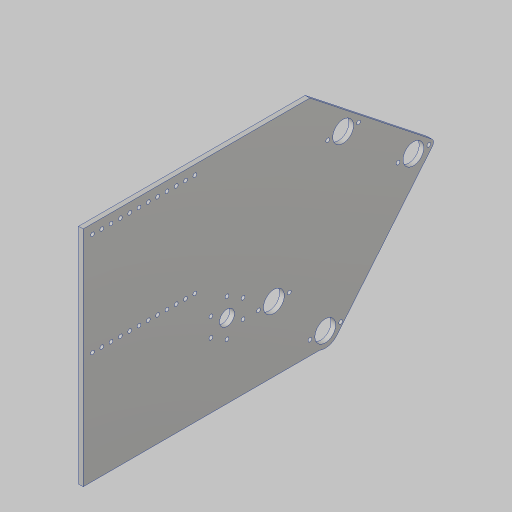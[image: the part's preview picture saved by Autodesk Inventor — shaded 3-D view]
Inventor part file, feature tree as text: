
AUTODESK INVENTOR PART (.ipt)
format: ipt  version: 2023.5 (Build 275446000, 446)  size: 254,976 bytes
history: native  units: in
note: dims shown in document units (in); Inventor stores cm internally (conversion verified against a paired STEP export)
features: sketch x4, extrude x2, hole x2, projected_geometry x2
ambient origin geometry x8: Origin, YZ Plane, XZ Plane, XY Plane, X Axis, Y Axis, Z Axis, Center Point
bodies: Solid1 (feature_tree)
feature tree (10):
  sketch  "Sketch2"  dims[d2=5.0in d3=3.0in]
  extrude  "Extrusion1"  Depth=3.0in
  sketch  "Sketch3"  dims[d4=0.5in d5=12.0in]
  sketch  "Sketch4"  dims[d6=4.5in d7=1.25in]
  extrude  "Extrusion2"  Depth=12.0in
  hole  "Hole1"  [1 undecoded]
  hole  "Hole3"  [1 undecoded]
  sketch  "Sketch6"  dims[d8=2.0in d9=5.0in d10=6.875in d11=1.115in d12=1.25in d13=1.0in d14=3.8976in d16=8.7496in d17=5.0in d18=4.7835in d27=7.0in d33=0.25in d34=0.0in d36=3.0in d37=5.0in d38=0.25in d40=2.0in d41=0.75in d42=16.0in d43=5.0in d44=0.313in d45=0.313in d46=1.5748in d48=1.0in d49=0.3937in d51=1.0in d53=0.8in d55=4.0in d56=1.0in d57=0.0in d58=2.0in d59=2.3622in d61=360.0deg d63=0.201in d64=0.75in d65=0.385in d66=0.25in d67=0.5635in d68=1.0in d69=0.8108in d70=7.1093in d80=1.655in d81=1.655in d82=1.655in d83=1.655in d84=0.5in d85=0.25in d86=0.25in d87=0.25in d89=0.201in d90=0.75in d91=0.385in d92=0.25in d93=0.5635in d94=1.0in d95=0.8108in d97=6.0in d98=0.5in d101=0.5in d102=4.7244in d104=0.5in d105=0.3937in d107=1.0in d109=4.5in d110=11.875in d111=0.75in d112=3.75in d113=12.0in d114=5.5in d115=5.0in d116=6.0in d117=2.5709in]
  projected_geometry  "Project Cut Edges1"
  projected_geometry  "Project Cut Edges2"
note: 2 required parameter values undecoded (feature->parameter linkage not recoverable at this tier; creation-order binding heuristic only, values carry confidence <= 0.55)
